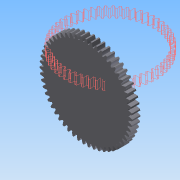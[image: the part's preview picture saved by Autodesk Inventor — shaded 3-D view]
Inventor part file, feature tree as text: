
AUTODESK INVENTOR PART (.ipt)
format: ipt  version: 2015 SP1 (Build 190203100, 203)  size: 364,544 bytes
history: native  units: mm (DEFAULTED — no unit token found)
features: plane x3, other x3, sketch x3, extrude x2
ambient origin geometry x8: Origin, YZ Plane, XZ Plane, XY Plane, X Axis, Y Axis, Z Axis, Center Point
bodies: Solid1 (feature_tree)
feature tree (11):
  extrude  "Extrusion1"  Depth=6.35mm TaperAngle=0.0deg
  plane  "Work Plane1"
  plane  "Work Plane2"
  plane  "Work Plane3"
  other  "Spur Gear"
  extrude  "Extrusion2"  Depth=76.2mm TaperAngle=0.0deg
  sketch  "Sketch1"  dims[d0=72.39mm d1=6.35mm d2=0.0mm]
  sketch  "Sketch2"  dims[d3=69.85mm d4=76.2mm d5=0.0mm]
  other  "Srf1"
  sketch  "Sketch3"  dims[d6=0.0mm d7=0.571199mm d9=0.0mm d14=0.0mm d15=41.91mm d16=0.0mm d17=0.0mm d18=0.0mm d19=41.91mm d20=9.5885mm d21=0.0mm d22=0.0mm]
  other  "Pitch Diameter"
